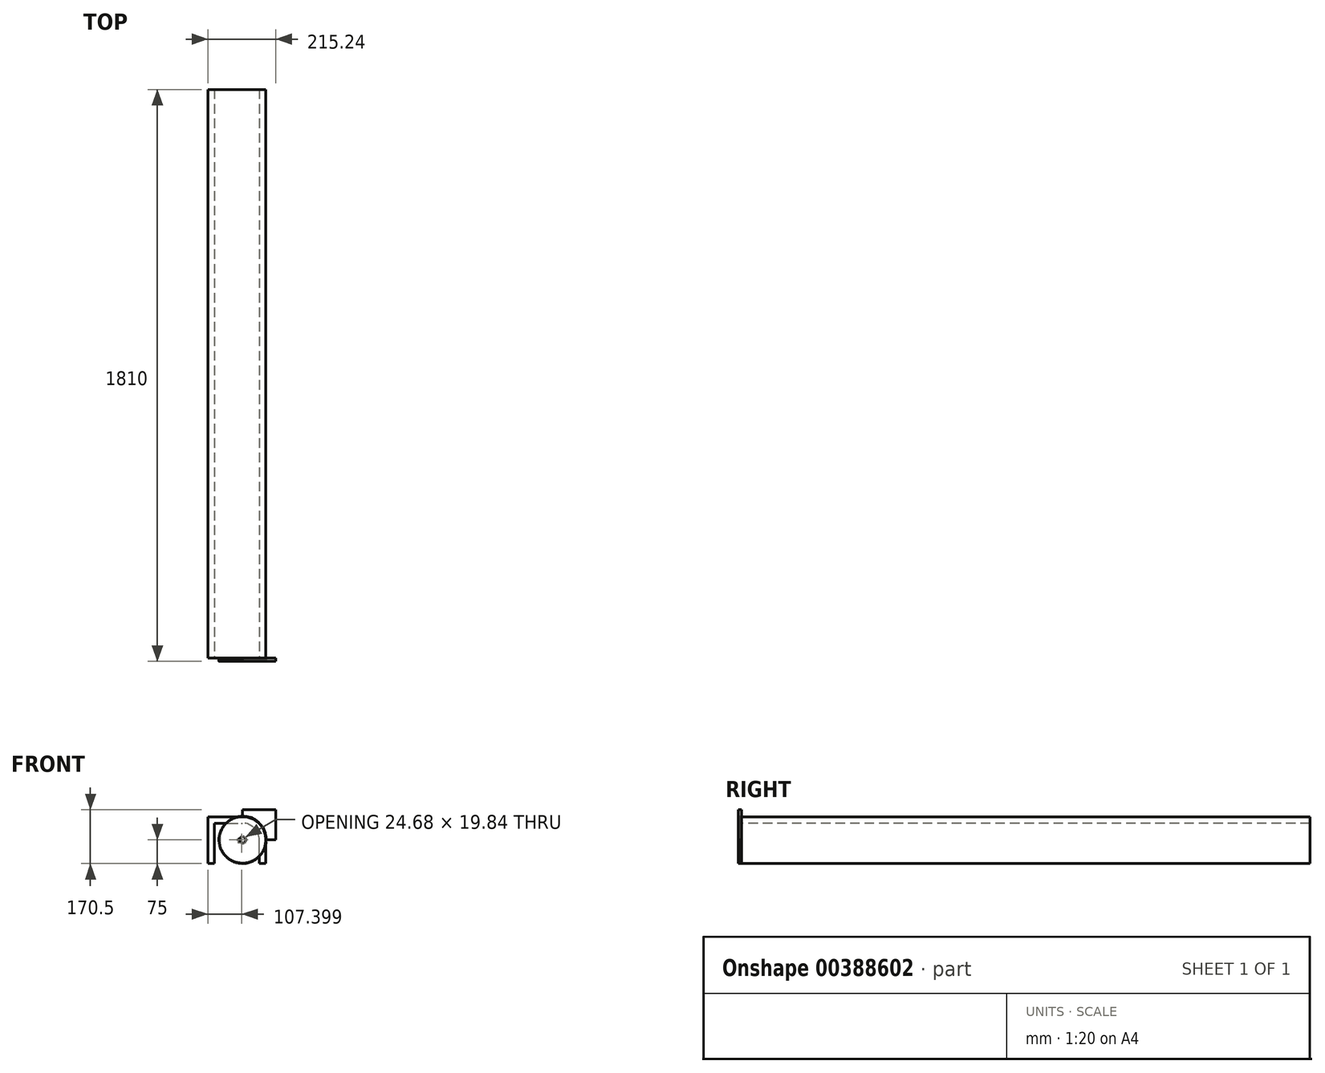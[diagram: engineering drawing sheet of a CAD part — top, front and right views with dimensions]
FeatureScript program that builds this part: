
annotation { "Feature Type Name" : "Feature", "Feature Type Description" : "" }
export const myFeature = defineFeature(function(context is Context, id is Id, definition is map)
    precondition{}
    {
        {
            var Q0;
            Q0=qCreatedBy(makeId("Front.planeOp"),FACE);
            var sketch = newSketch(context, id + "F0", { "sketchPlane" : qUnion([Q0])});
            skCircle(sketch, "E0", {"center": v(0, 0) * mm, "radius": 75 * mm});
            skLineSegment(sketch, "E1", {"start": v(0, 0) * mm, "end": v(75, 0) * mm, "construction": true});
            skLineSegment(sketch, "E2", {"start": v(75, 0) * mm, "end": v(73, 0) * mm, "construction": true});
            skLineSegment(sketch, "E3", {"start": v(0, 0) * mm, "end": v(74.97, -2.05) * mm, "construction": true});
            skLineSegment(sketch, "E4", {"start": v(74.97, -2.05) * mm, "end": v(72.97, -2) * mm, "construction": true});
            skLineSegment(sketch, "E5", {"start": v(73, 0) * mm, "end": v(72.97, -2) * mm, "construction": true});
            skArc(sketch, "E6", {"start": v(74, 0) * mm, "mid": v(73.09, -1) * mm, "end": v(73.97, -2.03) * mm});
            skLineSegment(sketch, "E7", {"start": v(75, 0) * mm, "end": v(74, 0) * mm});
            skLineSegment(sketch, "E8", {"start": v(74.97, -2.05) * mm, "end": v(73.97, -2.03) * mm});
            skPoint(sketch, "E9.center", {"position": v(25, -0.68) * mm});
            skLineSegment(sketch, "E9.anchor1", {"start": v(25, -0.68) * mm, "end": v(73.97, -2.03) * mm, "construction": true});
            skCircle(sketch, "E10", {"center": v(0, 0) * mm, "radius": 10 * mm});
            skLineSegment(sketch, "E11", {"start": v(0, 0) * mm, "end": v(-10, 0) * mm, "construction": true});
            skLineSegment(sketch, "E12.0", {"start": v(0, 2.5) * mm, "end": v(-10, 2.5) * mm, "construction": true});
            skLineSegment(sketch, "E13.0", {"start": v(0, -2.5) * mm, "end": v(-10, -2.5) * mm, "construction": true});
            skLineSegment(sketch, "E14", {"start": v(-9.68, -2.5) * mm, "end": v(-14.68, -2.5) * mm});
            skLineSegment(sketch, "E15", {"start": v(-14.68, -2.5) * mm, "end": v(-14.68, 2.5) * mm});
            skLineSegment(sketch, "E16", {"start": v(-14.68, 2.5) * mm, "end": v(-9.68, 2.5) * mm});
            skLineSegment(sketch, "E17", {"start": v(0, 75) * mm, "end": v(0, 75.5) * mm, "construction": true});
            skLineSegment(sketch, "E18", {"start": v(75, 0) * mm, "end": v(75.5, 0) * mm, "construction": true});
            skLineSegment(sketch, "E19", {"start": v(75.5, 0) * mm, "end": v(105.5, 0) * mm});
            skArc(sketch, "E20", {"start": v(75.5, 0) * mm, "mid": v(53.39, 53.39) * mm, "end": v(0, 75.5) * mm});
            skPoint(sketch, "E21.start.orphan", {"position": v(105.5, 75.5) * mm});
            skLineSegment(sketch, "E22", {"start": v(0, 75.5) * mm, "end": v(0, 95.5) * mm});
            skLineSegment(sketch, "E23", {"start": v(0, 95.5) * mm, "end": v(105.5, 95.5) * mm});
            skLineSegment(sketch, "E24", {"start": v(105.5, 95.5) * mm, "end": v(105.5, 0) * mm});
            skSolve(sketch);
        }
        {
            var Q0;
            Q0=makeQuery(id+"F0.imprint","IMPRINT",FACE,{"disambiguationData":[TD([[makeQuery(id+"F0.imprint","IMPRINT",EDGE,{"derivedFrom":sQuery(id+"F0.wireOp",EDGE,"E6")}),-1.0]])]});
            var Q1;
            Q1=makeQuery(id+"F0.imprint","IMPRINT",FACE,{"disambiguationData":[TD([[makeQuery(id+"F0.imprint","IMPRINT",EDGE,{"derivedFrom":sQuery(id+"F0.wireOp",EDGE,"NEatLMy0-6dVt-TztR-B6vm-dya0t83PIEw9")}),-1.0]])]});
            var Q2;
            Q2=makeQuery(id+"F0.imprint","IMPRINT",FACE,{"disambiguationData":[TD([[makeQuery(id+"F0.imprint","IMPRINT",EDGE,{"derivedFrom":sQuery(id+"F0.wireOp",EDGE,"E19")}),1.0]])]});
            extrude(context, id + "F1", {"entities" : qUnion([Q0, Q1, Q2]), "depth" : 10 * mm});
        }
        {
            var Q0;
            Q0=makeQuery(id+"F1.opExtrude","SWEPT_BODY",BODY,{"disambiguationData":[OSD([sQuery(id+"F0.wireOp",EDGE,"E0"),sQuery(id+"F0.wireOp",EDGE,"E9.299.0"),sQuery(id+"F0.wireOp",EDGE,"E9.299.1"),sQuery(id+"F0.wireOp",EDGE,"E9.299.2")])]});
            var Q1;
            Q1=makeQuery(id+"F1.opExtrude","SWEPT_FACE",FACE,{"disambiguationData":[OSD([sQuery(id+"F0.wireOp",EDGE,"E6")])]});
            var Q2;
            Q2=makeQuery(id+"F1.opExtrude","SWEPT_FACE",FACE,{"disambiguationData":[OSD([sQuery(id+"F0.wireOp",EDGE,"E7")])]});
            var Q3;
            Q3=makeQuery(id+"F1.opExtrude","SWEPT_FACE",FACE,{"disambiguationData":[OSD([sQuery(id+"F0.wireOp",EDGE,"E8")])]});
            var Q4;
            Q4=makeQuery(id+"F1.opExtrude","SWEPT_FACE",FACE,{"disambiguationData":[OSD([sQuery(id+"F0.wireOp",EDGE,"E0")])]});
            circularPattern(context, id + "F2", {"patternType" : PatternType.FACE, "faces" : qUnion([Q1, Q2, Q3]), "axis" : qUnion([Q4]), "angle" : 360 * degree, "instanceCount" : 120, "equalSpace" : true});
        }
        {
            var Q0;
            Q0=makeQuery(id+"F1.opExtrude","CAP_FACE",FACE,{"disambiguationData":[OSD([sQuery(id+"F0.wireOp",EDGE,"E0"),sQuery(id+"F0.wireOp",EDGE,"E6"),sQuery(id+"F0.wireOp",EDGE,"E7"),sQuery(id+"F0.wireOp",EDGE,"E8"),sQuery(id+"F0.wireOp",EDGE,"E10"),sQuery(id+"F0.wireOp",EDGE,"E14"),sQuery(id+"F0.wireOp",EDGE,"E15"),sQuery(id+"F0.wireOp",EDGE,"E16")])],"isStart":true});
            var sketch = newSketch(context, id + "F3", { "sketchPlane" : qUnion([Q0])});
            skLineSegment(sketch, "E25", {"start": v(-53, -74.97) * mm, "end": v(-53, 0) * mm});
            skLineSegment(sketch, "E26", {"start": v(89.74, 53) * mm, "end": v(0, 53) * mm});
            skLineSegment(sketch, "E27.0", {"start": v(0, 73) * mm, "end": v(109.74, 73) * mm});
            skArc(sketch, "E27.1", {"start": v(0, 73) * mm, "mid": v(-51.62, 51.62) * mm, "end": v(-73, 0) * mm});
            skLineSegment(sketch, "E27.2", {"start": v(-73, 0) * mm, "end": v(-73, -74.97) * mm});
            skLineSegment(sketch, "E28", {"start": v(-73, -74.97) * mm, "end": v(-53, -74.97) * mm});
            skLineSegment(sketch, "E29", {"start": v(109.74, 73) * mm, "end": v(109.74, 53) * mm});
            skLineSegment(sketch, "E30", {"start": v(109.74, 53) * mm, "end": v(109.74, -74.97) * mm});
            skLineSegment(sketch, "E31", {"start": v(109.74, -74.97) * mm, "end": v(89.74, -74.97) * mm});
            skLineSegment(sketch, "E32", {"start": v(89.74, -74.97) * mm, "end": v(89.74, 53) * mm});
            skArc(sketch, "E33", {"start": v(0, 53) * mm, "mid": v(-37.48, 37.48) * mm, "end": v(-53, 0) * mm});
            skSolve(sketch);
        }
        {
            var Q0;
            Q0 = qSketchRegion(id + "F3", true);
            extrude(context, id + "F4", {"entities" : qUnion([Q0]), "depth" : 1800 * mm});
        }
        {
            var Q0;
            Q0=makeQuery(id+"F1.opExtrude","SWEPT_EDGE",EDGE,{"disambiguationData":[OSD([sQuery(id+"F0.wireOp",EDGE,"E20"),sQuery(id+"F0.wireOp",EDGE,"E22")])]});
            fillet(context, id + "F5", {"entities" : qUnion([Q0]), "radius" : 5 * mm, "tangentPropagation" : true, "allowEdgeOverflow" : false});
        }
    });
